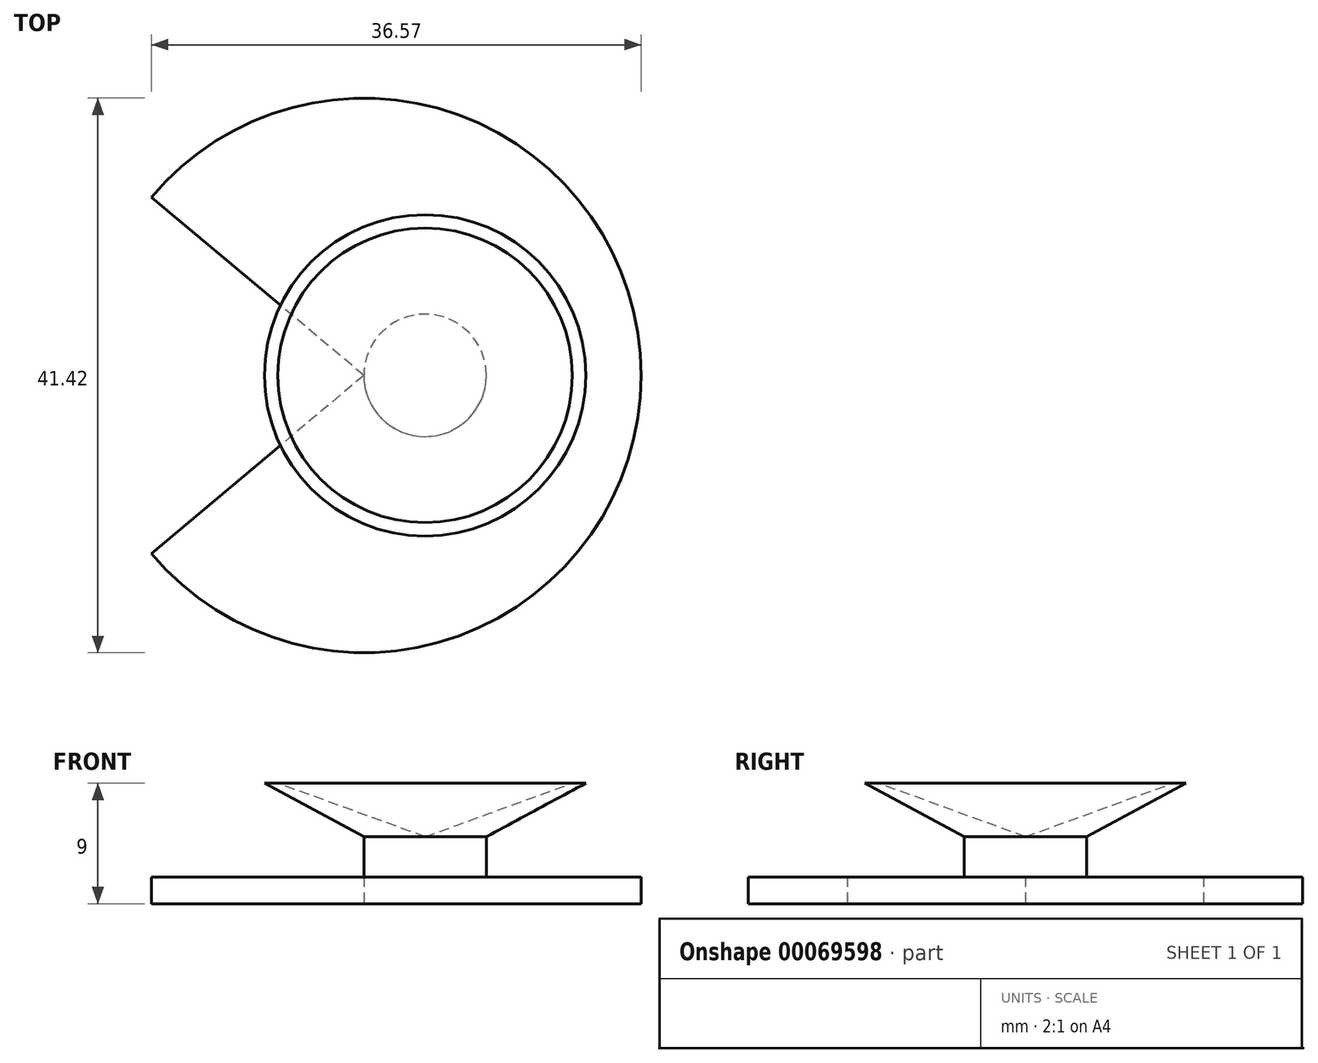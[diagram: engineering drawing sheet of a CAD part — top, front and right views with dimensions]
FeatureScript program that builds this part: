
annotation { "Feature Type Name" : "Feature", "Feature Type Description" : "" }
export const myFeature = defineFeature(function(context is Context, id is Id, definition is map)
    precondition{}
    {
        {
            var Q0;
            Q0=qCreatedBy(makeId("Top.planeOp"),FACE);
            var sketch = newSketch(context, id + "F0", { "sketchPlane" : qUnion([Q0])});
            skCircle(sketch, "E0", {"center": v(0, 0) * mm, "radius": 20.7 * mm});
            skLineSegment(sketch, "E1", {"start": v(0, 0) * mm, "end": v(-15.86, 13.31) * mm});
            skLineSegment(sketch, "E2", {"start": v(0, 0) * mm, "end": v(-15.86, -13.31) * mm});
            skLineSegment(sketch, "E3", {"start": v(0, 0) * mm, "end": v(-20.7, 0) * mm, "construction": true});
            skSolve(sketch);
        }
        {
            var Q0;
            {var subQ0=sQuery(id+"F0.wireOp",EDGE,"E1");Q0=makeQuery(id+"F0.imprint","IMPRINT",FACE,{"disambiguationData":[TD([[makeQuery(id+"F0.imprint","IMPRINT",EDGE,{"derivedFrom":subQ0}),-1.0]])]});}
            extrude(context, id + "F1", {"entities" : qUnion([Q0]), "depth" : 2 * mm});
        }
        {
            var Q0;
            Q0=makeQuery(id+"F1.opExtrude","CAP_FACE",FACE,{"disambiguationData":[OSD([sQuery(id+"F0.wireOp",EDGE,"E0"),sQuery(id+"F0.wireOp",EDGE,"E1"),sQuery(id+"F0.wireOp",EDGE,"E2")])],"isStart":false});
            var sketch = newSketch(context, id + "F2", { "sketchPlane" : qUnion([Q0])});
            skCircle(sketch, "E4", {"center": v(4.58, 0) * mm, "radius": 4.58 * mm});
            skSolve(sketch);
        }
        {
            var Q0;
            Q0 = qSketchRegion(id + "F2", true);
            extrude(context, id + "F3", {"entities" : qUnion([Q0]), "operationType" : NewBodyOperationType.ADD, "depth" : 3 * mm});
        }
        {
            var Q0;
            Q0=makeQuery(id+"F3.opExtrude","CAP_FACE",FACE,{"disambiguationData":[OSD([sQuery(id+"F2.wireOp",EDGE,"E4")])],"isStart":false});
            cPlane(context, id + "F4", {"entities" : qUnion([Q0]), "cplaneType" : CPlaneType.OFFSET, "offset" : 4 * mm, "width" : 150 * mm, "height" : 150 * mm});
        }
        {
            var Q0;
            Q0=qCreatedBy(id+"F4.planeOp",FACE);
            var sketch = newSketch(context, id + "F5", { "sketchPlane" : qUnion([Q0])});
            skCircle(sketch, "E5.0", {"center": v(4.58, 0) * mm, "radius": 4.58 * mm, "construction": true});
            skCircle(sketch, "E6", {"center": v(4.58, 0) * mm, "radius": 12 * mm});
            skSolve(sketch);
        }
        {
            var Q0;
            Q0=makeQuery(id+"F3.opExtrude","CAP_FACE",FACE,{"disambiguationData":[OSD([sQuery(id+"F2.wireOp",EDGE,"E4")])],"isStart":false});
            var sketch = newSketch(context, id + "F6", { "sketchPlane" : qUnion([Q0])});
            skPoint(sketch, "E7", {"position": v(4.58, 0) * mm});
            skSolve(sketch);
        }
        {
            var Q1;
            Q1=makeQuery(id+"F5.imprint","IMPRINT",FACE,{"disambiguationData":[TD([[makeQuery(id+"F5.imprint","IMPRINT",EDGE,{"derivedFrom":sQuery(id+"F5.wireOp",EDGE,"E6")}),1.0]])]});
            var Q2;
            Q2=makeQuery(id+"F3.opExtrude","CAP_FACE",FACE,{"disambiguationData":[OSD([sQuery(id+"F2.wireOp",EDGE,"E4")])],"isStart":false});
            loft(context, id + "F7", {"operationType" : NewBodyOperationType.ADD, "sheetProfilesArray" : [{ "sheetProfileEntities" : qUnion([Q1]) }, { "sheetProfileEntities" : qUnion([Q2]) }]});
        }
        {
            var Q0;
            Q0=makeQuery(id+"F7.opLoft","CAP_FACE",FACE,{"disambiguationData":[OSD([makeQuery(id+"F5.imprint","IMPRINT",FACE,{"disambiguationData":[TD([[makeQuery(id+"F5.imprint","IMPRINT",EDGE,{"derivedFrom":sQuery(id+"F5.wireOp",EDGE,"E6")}),1.0]])]})])],"isStart":true});
            var sketch = newSketch(context, id + "F8", { "sketchPlane" : qUnion([Q0])});
            skCircle(sketch, "E8", {"center": v(4.58, 0) * mm, "radius": 11 * mm});
            skLineSegment(sketch, "E9", {"start": v(4.58, 11) * mm, "end": v(4.58, 12) * mm, "construction": true});
            skSolve(sketch);
        }
        {
            var Q1;
            Q1=makeQuery(id+"F8.imprint","IMPRINT",FACE,{"disambiguationData":[TD([[makeQuery(id+"F8.imprint","IMPRINT",EDGE,{"derivedFrom":sQuery(id+"F8.wireOp",EDGE,"E8")}),1.0]])]});
            var Q2;
            Q2=sQuery(id+"F6.wireOp",VERTEX,"E7");
            loft(context, id + "F9", {"operationType" : NewBodyOperationType.REMOVE, "sheetProfilesArray" : [{ "sheetProfileEntities" : qUnion([Q1]) }, { "sheetProfileEntities" : qUnion([Q2]) }]});
        }
    });
